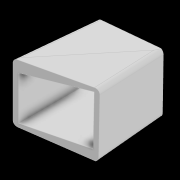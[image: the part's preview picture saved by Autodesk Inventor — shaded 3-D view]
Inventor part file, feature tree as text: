
AUTODESK INVENTOR PART (.ipt)
format: ipt  version: 2020.4 (Build 244396010, 396A)  size: 204,800 bytes
history: native  units: in
note: dims shown in document units (in); Inventor stores cm internally (conversion verified against a paired STEP export)
features: other x5, plane x4, surface_op x4, sketch x4, loft x2, boolean_combine x2, direct_edit x2, fillet x1
ambient origin geometry x8: Origin, YZ Plane, XZ Plane, XY Plane, X Axis, Y Axis, Z Axis, Center Point
bodies: Solid2 (feature_tree), Solid3 (feature_tree), Solid1 (feature_tree)
feature tree (24):
  other  "handle_top_final.ipt"
  loft  "Loft1"
  plane  "Work Plane14"
  plane  "Work Plane15"
  boolean_combine  "Combine6"
  surface_op  "Sculpt12"
  surface_op  "Sculpt13"
  direct_edit  "Direct Edit1"
  loft  "Loft2"
  plane  "Work Plane16"
  plane  "Work Plane17"
  boolean_combine  "Combine7"
  surface_op  "Sculpt14"
  surface_op  "Sculpt15"
  direct_edit  "Direct Edit2"
  fillet  "Fillet3"  Radius=0.1378in
  other  "Volumenkörper1::handle_top_final.ipt"
  other  "TaggingFeature1"
  sketch  "Sketch1"  dims[d0=0.3937in d3=0.1378in]
  sketch  "Sketch2"  dims[d4=0.2559in d5=0.1378in d6=0.1378in]
  sketch  "Sketch5"  dims[d7=0.0in d8=90.0deg]
  sketch  "Sketch6"  dims[d9=0.0in d10=90.0deg d13=0.1378in d14=0.2559in d15=0.1378in d16=0.1378in d17=0.0in d18=90.0deg d19=0.0in d20=90.0deg d22=0.1181in]
  other  "Delete1"
  other  "Delete2"
